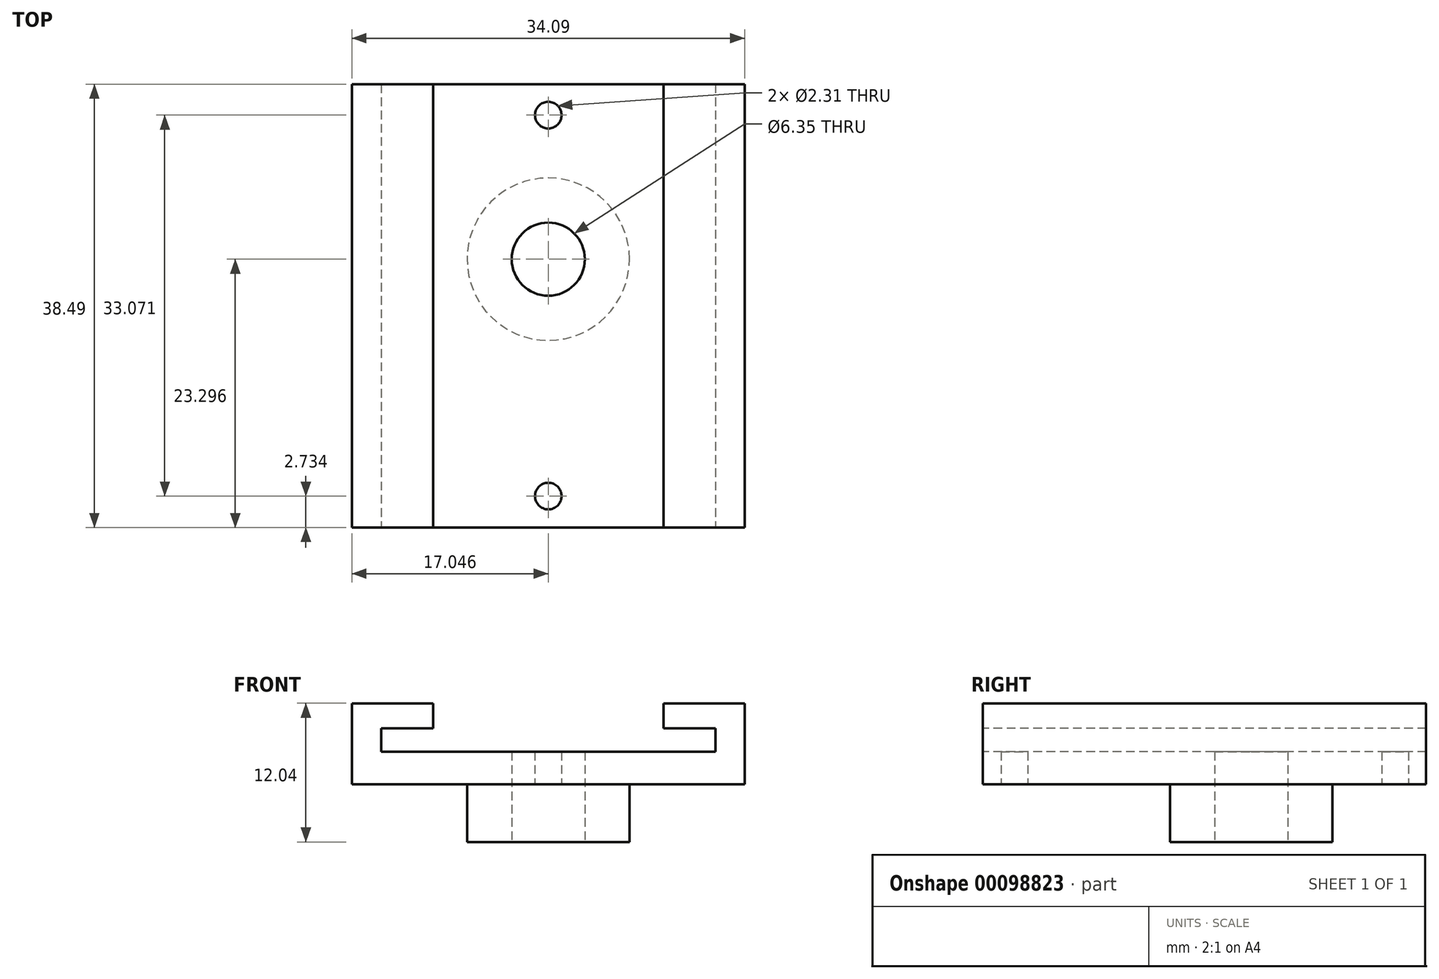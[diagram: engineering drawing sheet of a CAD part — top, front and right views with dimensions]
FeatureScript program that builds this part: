
annotation { "Feature Type Name" : "Feature", "Feature Type Description" : "" }
export const myFeature = defineFeature(function(context is Context, id is Id, definition is map)
    precondition{}
    {
        {
            var Q0;
            Q0=qCreatedBy(makeId("Top.planeOp"),FACE);
            var sketch = newSketch(context, id + "F0", { "sketchPlane" : qUnion([Q0])});
            skLineSegment(sketch, "E0.bottom", {"start": v(-44.4, 49.7) * mm, "end": v(-10.31, 49.7) * mm});
            skLineSegment(sketch, "E0.top", {"start": v(-44.4, 11.21) * mm, "end": v(-10.31, 11.21) * mm});
            skLineSegment(sketch, "E0.left", {"start": v(-44.4, 49.7) * mm, "end": v(-44.4, 11.21) * mm});
            skLineSegment(sketch, "E0.right", {"start": v(-10.31, 49.7) * mm, "end": v(-10.31, 11.21) * mm});
            skSolve(sketch);
        }
        {
            var Q0;
            Q0 = qSketchRegion(id + "F0", true);
            extrude(context, id + "F1", {"entities" : qUnion([Q0]), "depth" : 7.04 * mm});
        }
        {
            var Q0;
            Q0=makeQuery(id+"F1.opExtrude","SWEPT_FACE",FACE,{"disambiguationData":[OSD([sQuery(id+"F0.wireOp",EDGE,"E0.top")])]});
            var sketch = newSketch(context, id + "F2", { "sketchPlane" : qUnion([Q0])});
            skLineSegment(sketch, "E1.bottom", {"start": v(-37.36, 7.04) * mm, "end": v(-17.35, 7.04) * mm});
            skLineSegment(sketch, "E1.top", {"start": v(-37.36, 4.85) * mm, "end": v(-17.35, 4.85) * mm});
            skLineSegment(sketch, "E1.left", {"start": v(-37.36, 7.04) * mm, "end": v(-37.36, 4.85) * mm});
            skLineSegment(sketch, "E1.right", {"start": v(-17.35, 7.04) * mm, "end": v(-17.35, 4.85) * mm});
            skLineSegment(sketch, "E2", {"start": v(-27.35, 0) * mm, "end": v(-27.35, 7.04) * mm, "construction": true});
            skPoint(sketch, "E3", {"position": v(-27.35, 7.04) * mm});
            skSolve(sketch);
        }
        {
            var Q0;
            Q0 = qSketchRegion(id + "F2", true);
            extrude(context, id + "F3", {"entities" : qUnion([Q0]), "operationType" : NewBodyOperationType.REMOVE, "endBound" : BoundingType.THROUGH_ALL, "oppositeDirection" : true, "depth" : 25.4 * mm});
        }
        {
            var Q0;
            Q0=makeQuery(id+"F1.opExtrude","SWEPT_FACE",FACE,{"disambiguationData":[OSD([sQuery(id+"F0.wireOp",EDGE,"E0.top")])]});
            var sketch = newSketch(context, id + "F4", { "sketchPlane" : qUnion([Q0])});
            skLineSegment(sketch, "E4.bottom", {"start": v(-41.87, 4.85) * mm, "end": v(-12.84, 4.85) * mm});
            skLineSegment(sketch, "E4.top", {"start": v(-41.87, 2.82) * mm, "end": v(-12.84, 2.82) * mm});
            skLineSegment(sketch, "E4.left", {"start": v(-41.87, 4.85) * mm, "end": v(-41.87, 2.82) * mm});
            skLineSegment(sketch, "E4.right", {"start": v(-12.84, 4.85) * mm, "end": v(-12.84, 2.82) * mm});
            skLineSegment(sketch, "E5", {"start": v(-27.35, 0) * mm, "end": v(-27.35, 4.85) * mm, "construction": true});
            skPoint(sketch, "E6", {"position": v(-27.35, 2.82) * mm});
            skPoint(sketch, "E7", {"position": v(-27.35, 4.85) * mm});
            skSolve(sketch);
        }
        {
            var Q0;
            Q0 = qSketchRegion(id + "F4", true);
            extrude(context, id + "F5", {"entities" : qUnion([Q0]), "operationType" : NewBodyOperationType.REMOVE, "endBound" : BoundingType.THROUGH_ALL, "oppositeDirection" : true, "depth" : 25.4 * mm});
        }
        {
            var Q0;
            Q0=makeQuery(id+"F1.opExtrude","CAP_FACE",FACE,{"disambiguationData":[OSD([sQuery(id+"F0.wireOp",EDGE,"E0.bottom"),sQuery(id+"F0.wireOp",EDGE,"E0.top"),sQuery(id+"F0.wireOp",EDGE,"E0.left"),sQuery(id+"F0.wireOp",EDGE,"E0.right")])],"isStart":true});
            var sketch = newSketch(context, id + "F6", { "sketchPlane" : qUnion([Q0])});
            skLineSegment(sketch, "E8", {"start": v(-27.35, -11.21) * mm, "end": v(-27.35, -49.7) * mm, "construction": true});
            skCircle(sketch, "E9", {"center": v(-27.35, -13.94) * mm, "radius": 1.16 * mm});
            skCircle(sketch, "E10", {"center": v(-27.35, -34.5) * mm, "radius": 3.18 * mm});
            skCircle(sketch, "E11", {"center": v(-27.35, -47.02) * mm, "radius": 1.16 * mm});
            skPoint(sketch, "E12", {"position": v(-27.35, -15.1) * mm});
            skPoint(sketch, "E13", {"position": v(-27.35, -37.68) * mm});
            skPoint(sketch, "E14", {"position": v(-27.35, -48.17) * mm});
            skSolve(sketch);
        }
        {
            var Q0;
            Q0 = qSketchRegion(id + "F6", true);
            extrude(context, id + "F7", {"entities" : qUnion([Q0]), "operationType" : NewBodyOperationType.REMOVE, "oppositeDirection" : true, "depth" : 25.4 * mm});
        }
        {
            var Q0;
            Q0=makeQuery(id+"F1.opExtrude","CAP_FACE",FACE,{"disambiguationData":[OSD([sQuery(id+"F0.wireOp",EDGE,"E0.bottom"),sQuery(id+"F0.wireOp",EDGE,"E0.top"),sQuery(id+"F0.wireOp",EDGE,"E0.left"),sQuery(id+"F0.wireOp",EDGE,"E0.right")])],"isStart":true});
            var sketch = newSketch(context, id + "F8", { "sketchPlane" : qUnion([Q0])});
            skCircle(sketch, "E15", {"center": v(-27.35, -34.5) * mm, "radius": 7.05 * mm});
            skSolve(sketch);
        }
        {
            var Q0;
            Q0=makeQuery(id+"F8.imprint","IMPRINT",FACE,{"disambiguationData":[TD([[makeQuery(id+"F8.imprint","IMPRINT",EDGE,{"derivedFrom":sQuery(id+"F8.wireOp",EDGE,"E15")}),1.0]])]});
            extrude(context, id + "F9", {"entities" : qUnion([Q0]), "operationType" : NewBodyOperationType.ADD, "depth" : 5 * mm});
        }
    });
